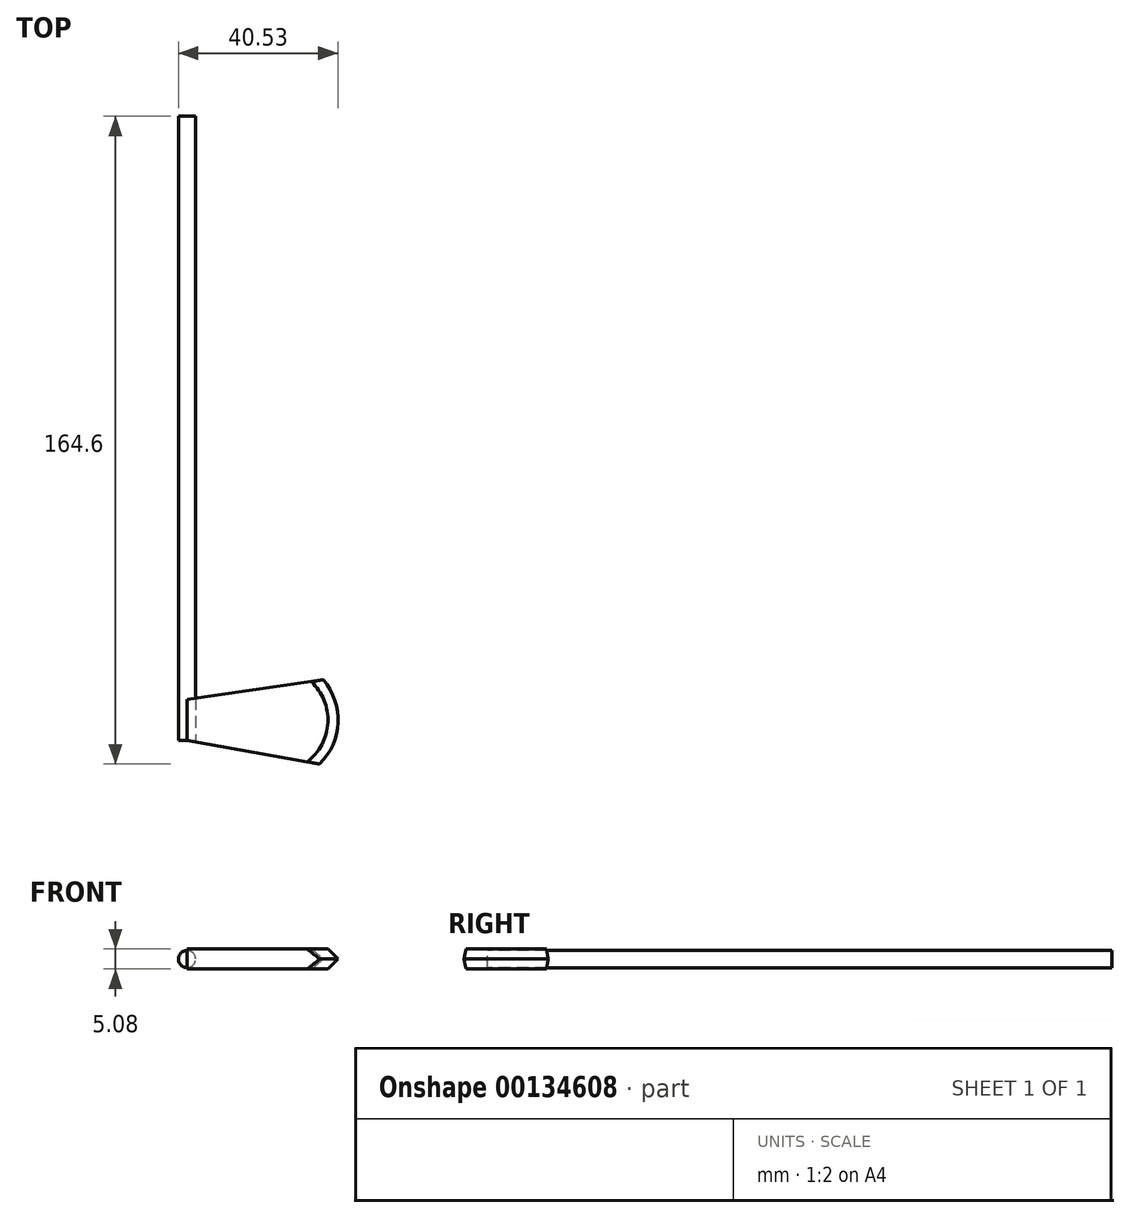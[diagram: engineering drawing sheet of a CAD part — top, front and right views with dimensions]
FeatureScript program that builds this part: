
annotation { "Feature Type Name" : "Feature", "Feature Type Description" : "" }
export const myFeature = defineFeature(function(context is Context, id is Id, definition is map)
    precondition{}
    {
        {
            var Q0;
            Q0=qCreatedBy(makeId("Front.planeOp"),FACE);
            var sketch = newSketch(context, id + "F0", { "sketchPlane" : qUnion([Q0])});
            skCircle(sketch, "E0", {"center": v(0, 0) * mm, "radius": 2.18 * mm});
            skSolve(sketch);
        }
        {
            var Q0;
            Q0 = qSketchRegion(id + "F0", true);
            extrude(context, id + "F1", {"entities" : qUnion([Q0]), "oppositeDirection" : true, "depth" : 158.65 * mm});
        }
        {
            var Q0;
            Q0=qCreatedBy(makeId("Top.planeOp"),FACE);
            var sketch = newSketch(context, id + "F2", { "sketchPlane" : qUnion([Q0])});
            skLineSegment(sketch, "E1", {"start": v(0, 0) * mm, "end": v(0, 21) * mm});
            skLineSegment(sketch, "E2", {"start": v(0, 0) * mm, "end": v(33.73, -5.95) * mm});
            skLineSegment(sketch, "E3", {"start": v(0, 10.5) * mm, "end": v(34.64, 15.46) * mm});
            skArc(sketch, "E4", {"start": v(33.73, -5.95) * mm, "mid": v(38.33, 4.58) * mm, "end": v(34.64, 15.46) * mm});
            skSolve(sketch);
        }
        {
            var Q0;
            Q0 = qSketchRegion(id + "F2", true);
            extrude(context, id + "F3", {"entities" : qUnion([Q0]), "depth" : 2.54 * mm, "hasSecondDirection" : true, "secondDirectionOppositeDirection" : true, "secondDirectionDepth" : 2.54 * mm});
        }
        {
            var Q0;
            Q0=makeQuery(id+"F3.opExtrude","CAP_EDGE",EDGE,{"disambiguationData":[OSD([sQuery(id+"F2.wireOp",EDGE,"E4")])],"isStart":true});
            var Q1;
            Q1=makeQuery(id+"F3.opExtrude","CAP_EDGE",EDGE,{"disambiguationData":[OSD([sQuery(id+"F2.wireOp",EDGE,"E4")])],"isStart":false});
            chamfer(context, id + "F4", {"entities" : qUnion([Q0, Q1]), "width" : 2.54 * mm, "tangentPropagation" : true});
        }
    });
